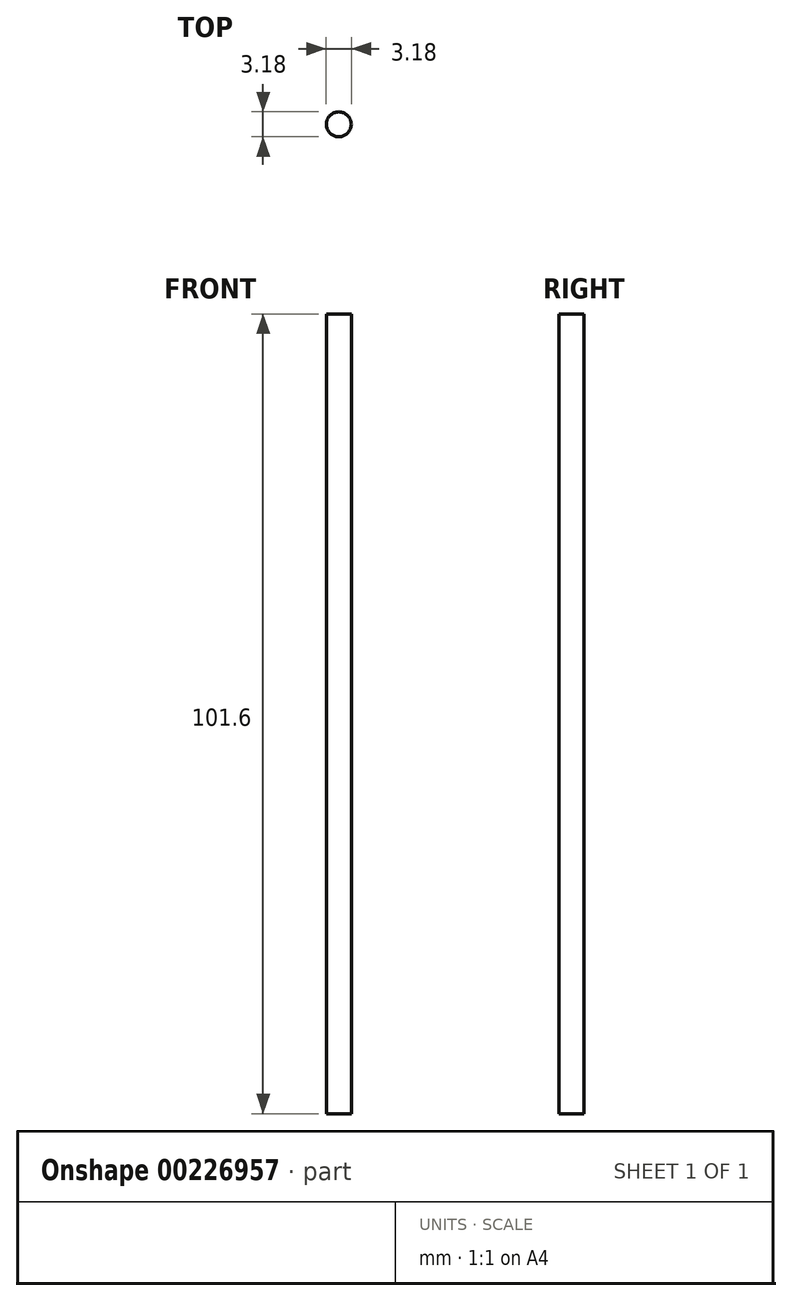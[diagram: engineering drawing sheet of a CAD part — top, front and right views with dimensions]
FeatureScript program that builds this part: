
annotation { "Feature Type Name" : "Feature", "Feature Type Description" : "" }
export const myFeature = defineFeature(function(context is Context, id is Id, definition is map)
    precondition{}
    {
        {
            var Q0;
            Q0=qCreatedBy(makeId("Top.planeOp"),FACE);
            var sketch = newSketch(context, id + "F0", { "sketchPlane" : qUnion([Q0])});
            skCircle(sketch, "E0", {"center": v(-45.68, 47.38) * mm, "radius": 1.59 * mm});
            skSolve(sketch);
        }
        {
            var Q0;
            Q0=makeQuery(id+"F0.imprint","IMPRINT",FACE,{"disambiguationData":[TD([[makeQuery(id+"F0.imprint","IMPRINT",EDGE,{"derivedFrom":sQuery(id+"F0.wireOp",EDGE,"E0")}),1.0]])]});
            extrude(context, id + "F1", {"entities" : qUnion([Q0]), "depth" : 101.6 * mm});
        }
    });
